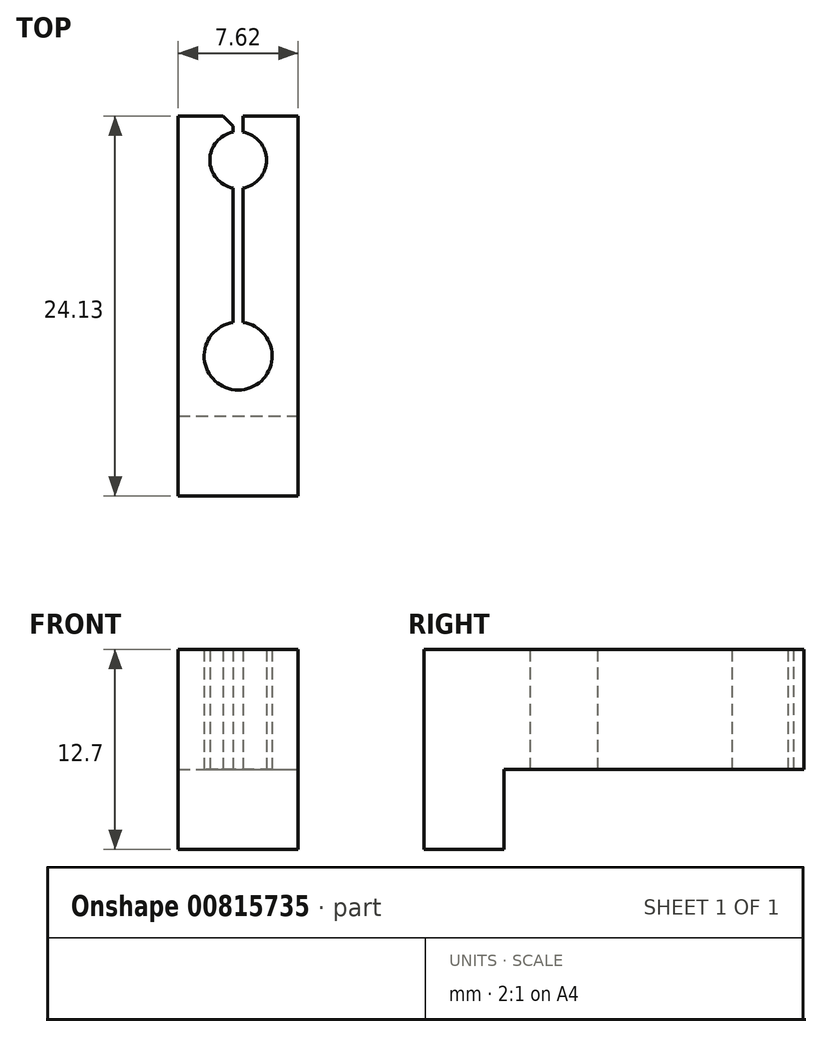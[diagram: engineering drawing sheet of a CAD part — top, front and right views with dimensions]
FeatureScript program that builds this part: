
annotation { "Feature Type Name" : "Feature", "Feature Type Description" : "" }
export const myFeature = defineFeature(function(context is Context, id is Id, definition is map)
    precondition{}
    {
        {
            var Q0;
            Q0=qCreatedBy(makeId("Top.planeOp"),FACE);
            var sketch = newSketch(context, id + "F0", { "sketchPlane" : qUnion([Q0])});
            skLineSegment(sketch, "E0.bottom", {"start": v(-3.81, 0) * mm, "end": v(3.81, 0) * mm});
            skLineSegment(sketch, "E0.top", {"start": v(-3.8, -24.13) * mm, "end": v(3.8, -24.13) * mm});
            skLineSegment(sketch, "E0.left", {"start": v(-3.8, 0) * mm, "end": v(-3.81, -24.13) * mm});
            skLineSegment(sketch, "E0.right", {"start": v(3.81, 0) * mm, "end": v(3.8, -24.13) * mm});
            skCircle(sketch, "E1", {"center": v(0, -2.8) * mm, "radius": 1.8 * mm});
            skCircle(sketch, "E2", {"center": v(0, -15.24) * mm, "radius": 2.16 * mm});
            skSolve(sketch);
        }
        {
            var Q0;
            Q0=qCreatedBy(makeId("Top.planeOp"),FACE);
            var sketch = newSketch(context, id + "F1", { "sketchPlane" : qUnion([Q0])});
            skLineSegment(sketch, "E3.bottom", {"start": v(-0.32, 0) * mm, "end": v(0.32, 0) * mm});
            skLineSegment(sketch, "E3.top", {"start": v(-0.32, -15.24) * mm, "end": v(0.32, -15.24) * mm});
            skLineSegment(sketch, "E3.left", {"start": v(-0.32, 0) * mm, "end": v(-0.32, -15.24) * mm});
            skLineSegment(sketch, "E3.right", {"start": v(0.32, 0) * mm, "end": v(0.32, -15.24) * mm});
            skSolve(sketch);
        }
        {
            var Q0;
            Q0 = qSketchRegion(id + "F0", true);
            extrude(context, id + "F2", {"entities" : qUnion([Q0]), "depth" : 12.7 * mm, "offsetDistance" : 25.4 * mm});
        }
        {
            var Q0;
            Q0 = qSketchRegion(id + "F1", true);
            extrude(context, id + "F3", {"entities" : qUnion([Q0]), "operationType" : NewBodyOperationType.REMOVE, "depth" : 19.05 * mm, "offsetDistance" : 25.4 * mm});
        }
        {
            var Q0;
            Q0=makeQuery(id+"F3.boolean.opBoolean","COPY",EDGE,{"derivedFrom":makeQuery(id+"F3.opExtrude","SWEPT_EDGE",EDGE,{"disambiguationData":[OSD([sQuery(id+"F1.wireOp",EDGE,"E3.bottom"),sQuery(id+"F1.wireOp",EDGE,"E3.right")])]})});
            var Q1;
            Q1=makeQuery(id+"F3.boolean.opBoolean","COPY",EDGE,{"derivedFrom":makeQuery(id+"F3.opExtrude","SWEPT_EDGE",EDGE,{"disambiguationData":[OSD([sQuery(id+"F1.wireOp",EDGE,"E3.bottom"),sQuery(id+"F1.wireOp",EDGE,"E3.left")])]})});
            chamfer(context, id + "F4", {"entities" : qUnion([Q0, Q1]), "width" : 0.64 * mm, "tangentPropagation" : true});
        }
        {
            var Q0;
            Q0=qCreatedBy(makeId("Right.planeOp"),FACE);
            var sketch = newSketch(context, id + "F5", { "sketchPlane" : qUnion([Q0])});
            skLineSegment(sketch, "E4.bottom", {"start": v(-19.05, 0) * mm, "end": v(0, 0) * mm});
            skLineSegment(sketch, "E4.top", {"start": v(-19.05, 5.08) * mm, "end": v(0, 5.08) * mm});
            skLineSegment(sketch, "E4.left", {"start": v(-19.05, 0) * mm, "end": v(-19.05, 5.08) * mm});
            skLineSegment(sketch, "E4.right", {"start": v(0, 0) * mm, "end": v(0, 5.08) * mm});
            skSolve(sketch);
        }
        {
            var Q0;
            Q0 = qSketchRegion(id + "F5", true);
            extrude(context, id + "F6", {"entities" : qUnion([Q0]), "operationType" : NewBodyOperationType.REMOVE, "endBound" : BoundingType.SYMMETRIC, "oppositeDirection" : true, "depth" : 25.4 * mm, "offsetDistance" : 25.4 * mm});
        }
    });
